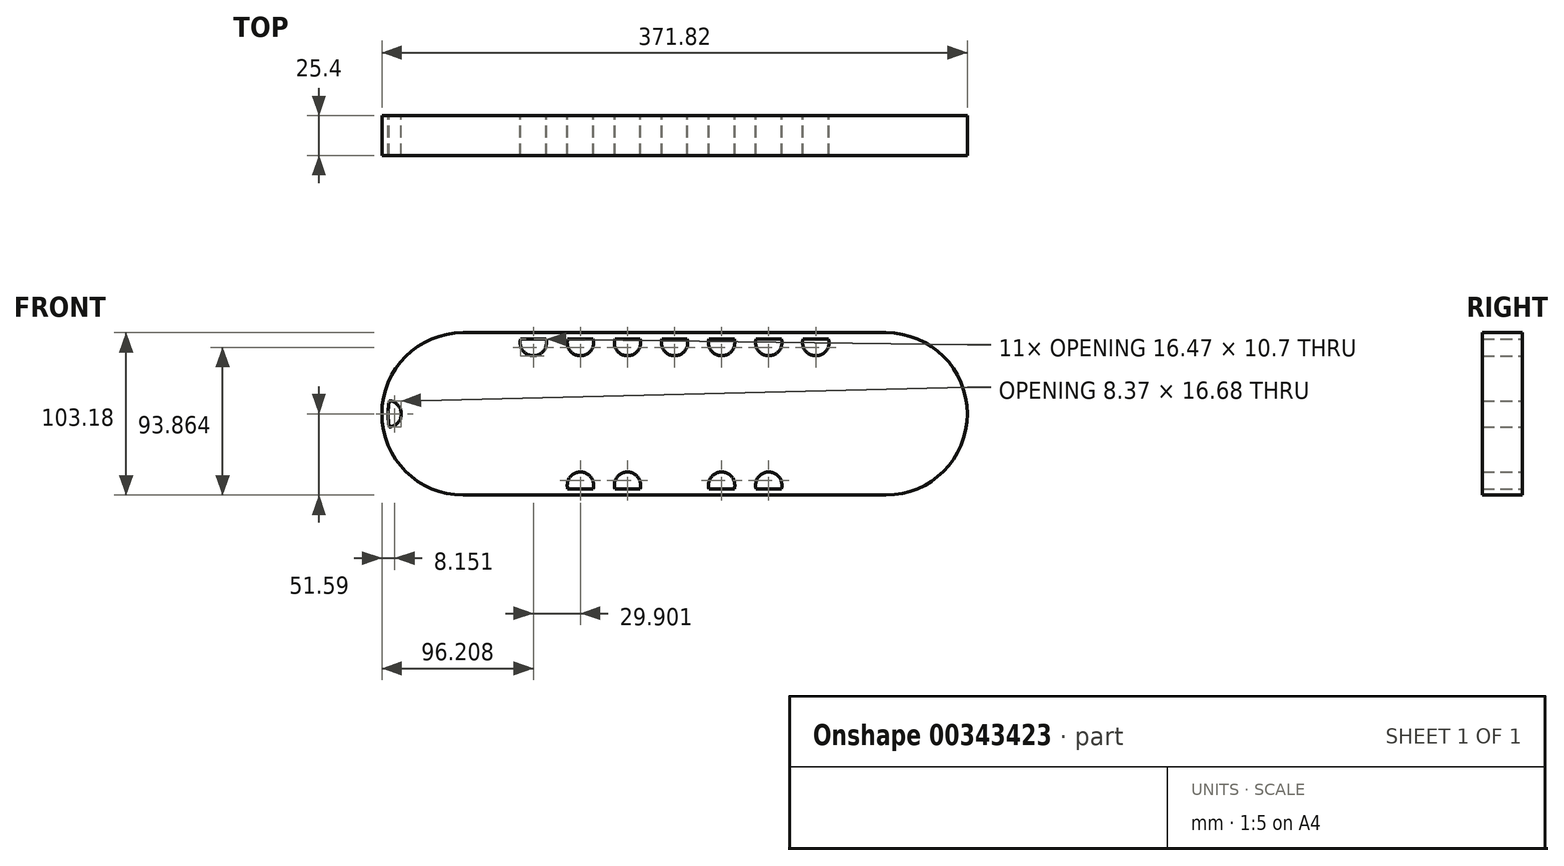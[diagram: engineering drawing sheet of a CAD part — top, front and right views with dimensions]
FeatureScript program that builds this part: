
annotation { "Feature Type Name" : "Feature", "Feature Type Description" : "" }
export const myFeature = defineFeature(function(context is Context, id is Id, definition is map)
    precondition{}
    {
        {
            var Q0;
            Q0=qCreatedBy(makeId("Front.planeOp"),FACE);
            var sketch = newSketch(context, id + "F0", { "sketchPlane" : qUnion([Q0])});
            skCircle(sketch, "E0", {"center": v(0, 0) * mm, "radius": 9.53 * mm});
            skCircle(sketch, "E1", {"center": v(0, 0) * mm, "radius": 15.88 * mm});
            skCircle(sketch, "E2", {"center": v(0, 0) * mm, "radius": 25.4 * mm});
            skCircle(sketch, "E3", {"center": v(0, 0) * mm, "radius": 38.1 * mm});
            skArc(sketch, "E4", {"start": v(5.87, 47.26) * mm, "mid": v(0, 47.63) * mm, "end": v(-5.87, 47.26) * mm});
            skLineSegment(sketch, "E5", {"start": v(-5.87, 47.26) * mm, "end": v(-7.62, 37.33) * mm});
            skLineSegment(sketch, "E6", {"start": v(5.87, 47.26) * mm, "end": v(7.62, 37.33) * mm});
            skLineSegment(sketch, "E7.1.0", {"start": v(-32.53, 34.79) * mm, "end": v(-28.1, 25.72) * mm});
            skArc(sketch, "E7.1.1", {"start": v(-23.03, 41.69) * mm, "mid": v(-28, 38.53) * mm, "end": v(-32.53, 34.79) * mm});
            skLineSegment(sketch, "E7.1.2", {"start": v(-23.03, 41.69) * mm, "end": v(-15.78, 34.68) * mm});
            skLineSegment(sketch, "E7.2.0", {"start": v(-46.76, 9.02) * mm, "end": v(-37.86, 4.29) * mm});
            skArc(sketch, "E7.2.1", {"start": v(-43.14, 20.19) * mm, "mid": v(-45.3, 14.72) * mm, "end": v(-46.76, 9.02) * mm});
            skLineSegment(sketch, "E7.2.2", {"start": v(-43.14, 20.19) * mm, "end": v(-33.15, 18.78) * mm});
            skLineSegment(sketch, "E7.3.0", {"start": v(-43.14, -20.19) * mm, "end": v(-33.15, -18.78) * mm});
            skArc(sketch, "E7.3.1", {"start": v(-46.76, -9.02) * mm, "mid": v(-45.3, -14.72) * mm, "end": v(-43.14, -20.19) * mm});
            skLineSegment(sketch, "E7.3.2", {"start": v(-46.76, -9.02) * mm, "end": v(-37.86, -4.29) * mm});
            skLineSegment(sketch, "E7.4.0", {"start": v(-23.03, -41.69) * mm, "end": v(-15.78, -34.68) * mm});
            skArc(sketch, "E7.4.1", {"start": v(-32.53, -34.79) * mm, "mid": v(-28, -38.53) * mm, "end": v(-23.03, -41.69) * mm});
            skLineSegment(sketch, "E7.4.2", {"start": v(-32.53, -34.79) * mm, "end": v(-28.1, -25.72) * mm});
            skLineSegment(sketch, "E7.5.0", {"start": v(5.87, -47.26) * mm, "end": v(7.62, -37.33) * mm});
            skArc(sketch, "E7.5.1", {"start": v(-5.87, -47.26) * mm, "mid": v(0, -47.63) * mm, "end": v(5.87, -47.26) * mm});
            skLineSegment(sketch, "E7.5.2", {"start": v(-5.87, -47.26) * mm, "end": v(-7.62, -37.33) * mm});
            skLineSegment(sketch, "E7.6.0", {"start": v(32.53, -34.79) * mm, "end": v(28.1, -25.72) * mm});
            skArc(sketch, "E7.6.1", {"start": v(23.03, -41.69) * mm, "mid": v(28, -38.53) * mm, "end": v(32.53, -34.79) * mm});
            skLineSegment(sketch, "E7.6.2", {"start": v(23.03, -41.69) * mm, "end": v(15.78, -34.68) * mm});
            skLineSegment(sketch, "E7.7.0", {"start": v(46.76, -9.02) * mm, "end": v(37.86, -4.29) * mm});
            skArc(sketch, "E7.7.1", {"start": v(43.14, -20.19) * mm, "mid": v(45.3, -14.72) * mm, "end": v(46.76, -9.02) * mm});
            skLineSegment(sketch, "E7.7.2", {"start": v(43.14, -20.19) * mm, "end": v(33.15, -18.78) * mm});
            skLineSegment(sketch, "E7.8.0", {"start": v(43.14, 20.19) * mm, "end": v(33.15, 18.78) * mm});
            skArc(sketch, "E7.8.1", {"start": v(46.76, 9.02) * mm, "mid": v(45.3, 14.72) * mm, "end": v(43.14, 20.19) * mm});
            skLineSegment(sketch, "E7.8.2", {"start": v(46.76, 9.02) * mm, "end": v(37.86, 4.29) * mm});
            skLineSegment(sketch, "E7.9.0", {"start": v(23.03, 41.69) * mm, "end": v(15.78, 34.68) * mm});
            skArc(sketch, "E7.9.1", {"start": v(32.53, 34.79) * mm, "mid": v(28, 38.53) * mm, "end": v(23.03, 41.69) * mm});
            skLineSegment(sketch, "E7.9.2", {"start": v(32.53, 34.79) * mm, "end": v(28.1, 25.72) * mm});
            skLineSegment(sketch, "E8", {"start": v(-3.98, 25.09) * mm, "end": v(-3.98, 15.37) * mm});
            skLineSegment(sketch, "E9", {"start": v(3.98, 25.09) * mm, "end": v(3.98, 15.37) * mm});
            skLineSegment(sketch, "E10.1.0", {"start": v(-19.74, -15.99) * mm, "end": v(-11.32, -11.13) * mm});
            skLineSegment(sketch, "E10.1.1", {"start": v(-23.71, -9.1) * mm, "end": v(-15.3, -4.24) * mm});
            skLineSegment(sketch, "E10.2.0", {"start": v(23.71, -9.1) * mm, "end": v(15.3, -4.24) * mm});
            skLineSegment(sketch, "E10.2.1", {"start": v(19.74, -15.99) * mm, "end": v(11.32, -11.13) * mm});
            skSolve(sketch);
        }
        {
            var Q0;
            Q0=qCreatedBy(makeId("Front.planeOp"),FACE);
            var sketch = newSketch(context, id + "F1", { "sketchPlane" : qUnion([Q0])});
            skArc(sketch, "E11", {"start": v(23.03, 41.69) * mm, "mid": v(-10.34, 46.49) * mm, "end": v(-38.53, 28) * mm});
            skLineSegment(sketch, "E12.0", {"start": v(23.03, 41.69) * mm, "end": v(15.78, 34.68) * mm, "construction": true});
            skLineSegment(sketch, "E12.1", {"start": v(5.87, 47.26) * mm, "end": v(7.62, 37.33) * mm, "construction": true});
            skLineSegment(sketch, "E12.2", {"start": v(-5.87, 47.26) * mm, "end": v(-7.62, 37.33) * mm, "construction": true});
            skLineSegment(sketch, "E12.3", {"start": v(-23.03, 41.69) * mm, "end": v(-15.78, 34.68) * mm, "construction": true});
            skLineSegment(sketch, "E12.4", {"start": v(-32.53, 34.79) * mm, "end": v(-28.1, 25.72) * mm, "construction": true});
            skLineSegment(sketch, "E12.5", {"start": v(-43.14, 20.19) * mm, "end": v(-33.15, 18.78) * mm, "construction": true});
            skLineSegment(sketch, "E12.6", {"start": v(-46.76, 9.02) * mm, "end": v(-37.86, 4.29) * mm, "construction": true});
            skLineSegment(sketch, "E12.7", {"start": v(-46.76, -9.02) * mm, "end": v(-37.86, -4.29) * mm, "construction": true});
            skLineSegment(sketch, "E13.0", {"start": v(-3.98, 25.09) * mm, "end": v(-3.98, 15.37) * mm, "construction": true});
            skLineSegment(sketch, "E13.1", {"start": v(3.98, 25.09) * mm, "end": v(3.98, 15.37) * mm, "construction": true});
            skLineSegment(sketch, "E13.2", {"start": v(23.71, -9.1) * mm, "end": v(15.3, -4.24) * mm, "construction": true});
            skLineSegment(sketch, "E13.3", {"start": v(19.74, -15.99) * mm, "end": v(11.32, -11.13) * mm, "construction": true});
            skLineSegment(sketch, "E13.4", {"start": v(-19.74, -15.99) * mm, "end": v(-11.32, -11.13) * mm, "construction": true});
            skLineSegment(sketch, "E13.5", {"start": v(-23.71, -9.1) * mm, "end": v(-15.3, -4.24) * mm, "construction": true});
            skCircle(sketch, "E14", {"center": v(14.72, 45.3) * mm, "radius": 8.37 * mm});
            skCircle(sketch, "E15", {"center": v(-14.72, 45.3) * mm, "radius": 8.37 * mm});
            skCircle(sketch, "E16", {"center": v(-38.53, 28) * mm, "radius": 8.37 * mm});
            skCircle(sketch, "E17", {"center": v(-47.62, 0) * mm, "radius": 8.37 * mm});
            skLineSegment(sketch, "E18", {"start": v(-14.72, 45.3) * mm, "end": v(14.72, 45.3) * mm, "construction": true});
            skArc(sketch, "E19.trimOffspring", {"start": v(-47.62, 0) * mm, "mid": v(-24.2, -41.02) * mm, "end": v(23.03, -41.69) * mm});
            skArc(sketch, "E20.trimOffspring", {"start": v(-42.84, 20.81) * mm, "mid": v(-45.3, 14.72) * mm, "end": v(-46.89, 8.34) * mm});
            skLineSegment(sketch, "E21", {"start": v(14.72, 45.3) * mm, "end": v(44.62, 45.3) * mm, "construction": true});
            skLineSegment(sketch, "E22", {"start": v(44.62, 45.3) * mm, "end": v(74.52, 45.3) * mm, "construction": true});
            skLineSegment(sketch, "E23", {"start": v(74.52, 45.3) * mm, "end": v(104.42, 45.3) * mm, "construction": true});
            skLineSegment(sketch, "E24", {"start": v(104.42, 45.3) * mm, "end": v(134.32, 45.3) * mm, "construction": true});
            skCircle(sketch, "E25", {"center": v(44.62, 45.3) * mm, "radius": 8.37 * mm});
            skCircle(sketch, "E26", {"center": v(74.52, 45.3) * mm, "radius": 8.37 * mm});
            skCircle(sketch, "E27", {"center": v(104.42, 45.3) * mm, "radius": 8.37 * mm});
            skCircle(sketch, "E28", {"center": v(134.32, 45.3) * mm, "radius": 8.37 * mm});
            skPoint(sketch, "E29", {"position": v(23.09, 45.3) * mm});
            skPoint(sketch, "E30", {"position": v(36.25, 45.3) * mm});
            skLineSegment(sketch, "E31", {"start": v(0, 0) * mm, "end": v(134.32, 0) * mm, "construction": true});
            skLineSegment(sketch, "E32", {"start": v(134.32, 45.3) * mm, "end": v(134.32, 0) * mm, "construction": true});
            skCircle(sketch, "E33.MirrorC", {"center": v(134.32, -45.3) * mm, "radius": 8.37 * mm});
            skCircle(sketch, "E34.MirrorC", {"center": v(104.42, -45.3) * mm, "radius": 8.37 * mm});
            skCircle(sketch, "E35.MirrorC", {"center": v(74.52, -45.3) * mm, "radius": 8.37 * mm});
            skCircle(sketch, "E36.MirrorC", {"center": v(44.62, -45.3) * mm, "radius": 8.37 * mm});
            skCircle(sketch, "E37.MirrorC", {"center": v(14.72, -45.3) * mm, "radius": 8.37 * mm});
            skCircle(sketch, "E38.MirrorC", {"center": v(-14.72, -45.3) * mm, "radius": 8.37 * mm});
            skCircle(sketch, "E39.MirrorC", {"center": v(-38.53, -28) * mm, "radius": 8.37 * mm});
            skCircle(sketch, "E40.MirrorC", {"center": v(164.22, -45.3) * mm, "radius": 8.37 * mm});
            skCircle(sketch, "E41.MirrorC", {"center": v(194.12, -45.3) * mm, "radius": 8.37 * mm});
            skCircle(sketch, "E42.MirrorC", {"center": v(224.03, -45.3) * mm, "radius": 8.37 * mm});
            skCircle(sketch, "E43.MirrorC", {"center": v(253.93, -45.3) * mm, "radius": 8.37 * mm});
            skCircle(sketch, "E44.MirrorC", {"center": v(283.36, -45.3) * mm, "radius": 8.37 * mm});
            skCircle(sketch, "E45.MirrorC", {"center": v(307.17, -28) * mm, "radius": 8.37 * mm});
            skCircle(sketch, "E46.MirrorC", {"center": v(316.27, 0) * mm, "radius": 8.37 * mm});
            skCircle(sketch, "E47.MirrorC", {"center": v(307.17, 28) * mm, "radius": 8.37 * mm});
            skCircle(sketch, "E48.MirrorC", {"center": v(283.36, 45.3) * mm, "radius": 8.37 * mm});
            skCircle(sketch, "E49.MirrorC", {"center": v(253.93, 45.3) * mm, "radius": 8.37 * mm});
            skCircle(sketch, "E50.MirrorC", {"center": v(224.03, 45.3) * mm, "radius": 8.37 * mm});
            skCircle(sketch, "E51.MirrorC", {"center": v(194.12, 45.3) * mm, "radius": 8.37 * mm});
            skCircle(sketch, "E52.MirrorC", {"center": v(164.22, 45.3) * mm, "radius": 8.37 * mm});
            skSolve(sketch);
        }
        {
            var Q0;
            Q0=qCreatedBy(makeId("Front.planeOp"),FACE);
            var sketch = newSketch(context, id + "F2", { "sketchPlane" : qUnion([Q0])});
            skArc(sketch, "E53", {"start": v(0, 47.62) * mm, "mid": v(-47.62, 0) * mm, "end": v(0, -47.62) * mm});
            skLineSegment(sketch, "E54", {"start": v(0, 47.62) * mm, "end": v(268.64, 47.62) * mm});
            skLineSegment(sketch, "E55", {"start": v(0, -47.62) * mm, "end": v(268.64, -47.62) * mm});
            skLineSegment(sketch, "E56.0", {"start": v(134.32, 45.3) * mm, "end": v(134.32, 0) * mm, "construction": true});
            skLineSegment(sketch, "E56.1", {"start": v(0, 0) * mm, "end": v(134.32, 0) * mm, "construction": true});
            skLineSegment(sketch, "E57.MirrorCS", {"start": v(268.64, 0) * mm, "end": v(134.32, 0) * mm, "construction": true});
            skArc(sketch, "E58", {"start": v(268.64, -47.62) * mm, "mid": v(316.27, 0) * mm, "end": v(268.64, 47.62) * mm});
            skLineSegment(sketch, "E59.0", {"start": v(0, 51.59) * mm, "end": v(268.64, 51.59) * mm});
            skArc(sketch, "E59.1", {"start": v(0, 51.59) * mm, "mid": v(-51.59, 0) * mm, "end": v(0, -51.59) * mm});
            skLineSegment(sketch, "E59.2", {"start": v(0, -51.59) * mm, "end": v(268.64, -51.59) * mm});
            skArc(sketch, "E59.3", {"start": v(268.64, -51.59) * mm, "mid": v(320.23, 0) * mm, "end": v(268.64, 51.59) * mm});
            skArc(sketch, "E60.0", {"start": v(69, 51.59) * mm, "mid": v(74.52, 36.92) * mm, "end": v(80.04, 51.59) * mm});
            skArc(sketch, "E60.1", {"start": v(98.9, 51.59) * mm, "mid": v(104.42, 36.92) * mm, "end": v(109.94, 51.59) * mm});
            skArc(sketch, "E60.2", {"start": v(139.84, 51.59) * mm, "mid": v(134.32, 36.92) * mm, "end": v(128.8, 51.59) * mm});
            skArc(sketch, "E60.3", {"start": v(169.74, 51.59) * mm, "mid": v(164.22, 36.92) * mm, "end": v(158.7, 51.59) * mm});
            skArc(sketch, "E60.4", {"start": v(199.65, 51.59) * mm, "mid": v(194.12, 36.92) * mm, "end": v(188.6, 51.59) * mm});
            skArc(sketch, "E60.5", {"start": v(229.55, 51.59) * mm, "mid": v(224.03, 36.92) * mm, "end": v(218.5, 51.59) * mm});
            skArc(sketch, "E60.6", {"start": v(259.45, 51.59) * mm, "mid": v(253.93, 36.92) * mm, "end": v(248.4, 51.59) * mm});
            skArc(sketch, "E60.7", {"start": v(39.1, 51.59) * mm, "mid": v(44.62, 36.92) * mm, "end": v(50.14, 51.59) * mm});
            skArc(sketch, "E60.8", {"start": v(9.2, 51.59) * mm, "mid": v(14.72, 36.92) * mm, "end": v(20.24, 51.59) * mm});
            skArc(sketch, "E60.9", {"start": v(-23.04, 46.15) * mm, "mid": v(-12.13, 37.33) * mm, "end": v(-8.49, 50.88) * mm});
            skArc(sketch, "E60.10", {"start": v(-45.77, 23.8) * mm, "mid": v(-31.76, 23.07) * mm, "end": v(-36.77, 36.18) * mm});
            skArc(sketch, "E60.11", {"start": v(-51.02, -7.65) * mm, "mid": v(-39.25, 0) * mm, "end": v(-51.02, 7.65) * mm});
            skArc(sketch, "E60.12", {"start": v(-45.77, -23.8) * mm, "mid": v(-31.76, -23.07) * mm, "end": v(-36.77, -36.18) * mm});
            skArc(sketch, "E60.13", {"start": v(9.2, -51.59) * mm, "mid": v(14.72, -36.92) * mm, "end": v(20.24, -51.59) * mm});
            skArc(sketch, "E60.14", {"start": v(39.1, -51.59) * mm, "mid": v(44.62, -36.92) * mm, "end": v(50.14, -51.59) * mm});
            skArc(sketch, "E60.15", {"start": v(69, -51.59) * mm, "mid": v(74.52, -36.92) * mm, "end": v(80.04, -51.59) * mm});
            skArc(sketch, "E60.16", {"start": v(98.9, -51.59) * mm, "mid": v(104.42, -36.92) * mm, "end": v(109.94, -51.59) * mm});
            skArc(sketch, "E60.17", {"start": v(128.8, -51.59) * mm, "mid": v(134.32, -36.92) * mm, "end": v(139.84, -51.59) * mm});
            skArc(sketch, "E60.18", {"start": v(169.74, -51.59) * mm, "mid": v(164.22, -36.92) * mm, "end": v(158.7, -51.59) * mm});
            skArc(sketch, "E60.19", {"start": v(229.55, -51.59) * mm, "mid": v(224.03, -36.92) * mm, "end": v(218.5, -51.59) * mm});
            skArc(sketch, "E60.20", {"start": v(259.45, -51.59) * mm, "mid": v(253.93, -36.92) * mm, "end": v(248.4, -51.59) * mm});
            skArc(sketch, "E60.21", {"start": v(291.69, -46.15) * mm, "mid": v(280.77, -37.33) * mm, "end": v(277.13, -50.88) * mm});
            skArc(sketch, "E60.22", {"start": v(199.65, -51.59) * mm, "mid": v(194.12, -36.92) * mm, "end": v(188.6, -51.59) * mm});
            skArc(sketch, "E60.23", {"start": v(314.42, -23.8) * mm, "mid": v(300.4, -23.07) * mm, "end": v(305.42, -36.18) * mm});
            skArc(sketch, "E60.24", {"start": v(319.66, -7.65) * mm, "mid": v(307.9, 0) * mm, "end": v(319.66, 7.65) * mm});
            skArc(sketch, "E60.25", {"start": v(314.42, 23.8) * mm, "mid": v(300.4, 23.07) * mm, "end": v(305.42, 36.18) * mm});
            skArc(sketch, "E60.26", {"start": v(291.69, 46.15) * mm, "mid": v(280.77, 37.33) * mm, "end": v(277.13, 50.88) * mm});
            skArc(sketch, "E60.27", {"start": v(-23.04, -46.15) * mm, "mid": v(-12.13, -37.33) * mm, "end": v(-8.49, -50.88) * mm});
            skSolve(sketch);
        }
        {
            var Q0;
            Q0 = qSketchRegion(id + "F2", true);
            var Q1;
            {var subQ0=sQuery(id+"F2.wireOp",EDGE,"E60.11");var subQ1=sQuery(id+"F2.wireOp",EDGE,"E53");var subQ2=makeQuery(id+"F2.imprint","INTERSECT",VERTEX,{"disambiguationData":[OD(0.0)],"derivedFrom":[subQ1,subQ0]});Q1=makeQuery(id+"F2.imprint","IMPRINT",FACE,{"disambiguationData":[TD([[makeQuery(id+"F2.imprint","IMPRINT",EDGE,{"disambiguationData":[TD([[subQ2,-1.0]])],"derivedFrom":subQ1}),1.0]])]});}
            var Q2;
            {var subQ0=sQuery(id+"F2.wireOp",EDGE,"E60.12");var subQ1=sQuery(id+"F2.wireOp",EDGE,"E53");var subQ2=makeQuery(id+"F2.imprint","INTERSECT",VERTEX,{"disambiguationData":[OD(0.0)],"derivedFrom":[subQ1,subQ0]});Q2=makeQuery(id+"F2.imprint","IMPRINT",FACE,{"disambiguationData":[TD([[makeQuery(id+"F2.imprint","IMPRINT",EDGE,{"disambiguationData":[TD([[subQ2,-1.0]])],"derivedFrom":subQ1}),1.0]])]});}
            var Q3;
            {var subQ0=sQuery(id+"F2.wireOp",EDGE,"E60.27");var subQ1=sQuery(id+"F2.wireOp",EDGE,"E53");var subQ2=makeQuery(id+"F2.imprint","INTERSECT",VERTEX,{"disambiguationData":[OD(0.0)],"derivedFrom":[subQ1,subQ0]});Q3=makeQuery(id+"F2.imprint","IMPRINT",FACE,{"disambiguationData":[TD([[makeQuery(id+"F2.imprint","IMPRINT",EDGE,{"disambiguationData":[TD([[subQ2,-1.0]])],"derivedFrom":subQ1}),1.0]])]});}
            var Q4;
            {var subQ0=sQuery(id+"F2.wireOp",EDGE,"E60.13");var subQ1=sQuery(id+"F2.wireOp",EDGE,"E55");var subQ2=makeQuery(id+"F2.imprint","INTERSECT",VERTEX,{"disambiguationData":[OD(0.0)],"derivedFrom":[subQ1,subQ0]});Q4=makeQuery(id+"F2.imprint","IMPRINT",FACE,{"disambiguationData":[TD([[makeQuery(id+"F2.imprint","IMPRINT",EDGE,{"disambiguationData":[TD([[subQ2,-1.0]])],"derivedFrom":subQ1}),1.0]])]});}
            var Q5;
            {var subQ0=sQuery(id+"F2.wireOp",EDGE,"E60.14");var subQ1=sQuery(id+"F2.wireOp",EDGE,"E55");var subQ2=makeQuery(id+"F2.imprint","INTERSECT",VERTEX,{"disambiguationData":[OD(0.0)],"derivedFrom":[subQ1,subQ0]});Q5=makeQuery(id+"F2.imprint","IMPRINT",FACE,{"disambiguationData":[TD([[makeQuery(id+"F2.imprint","IMPRINT",EDGE,{"disambiguationData":[TD([[subQ2,-1.0]])],"derivedFrom":subQ1}),1.0]])]});}
            var Q6;
            {var subQ0=sQuery(id+"F2.wireOp",EDGE,"E60.15");var subQ1=sQuery(id+"F2.wireOp",EDGE,"E55");var subQ2=makeQuery(id+"F2.imprint","INTERSECT",VERTEX,{"disambiguationData":[OD(0.0)],"derivedFrom":[subQ1,subQ0]});Q6=makeQuery(id+"F2.imprint","IMPRINT",FACE,{"disambiguationData":[TD([[makeQuery(id+"F2.imprint","IMPRINT",EDGE,{"disambiguationData":[TD([[subQ2,-1.0]])],"derivedFrom":subQ1}),1.0]])]});}
            var Q7;
            {var subQ0=sQuery(id+"F2.wireOp",EDGE,"E60.16");var subQ1=sQuery(id+"F2.wireOp",EDGE,"E55");var subQ2=makeQuery(id+"F2.imprint","INTERSECT",VERTEX,{"disambiguationData":[OD(0.0)],"derivedFrom":[subQ1,subQ0]});Q7=makeQuery(id+"F2.imprint","IMPRINT",FACE,{"disambiguationData":[TD([[makeQuery(id+"F2.imprint","IMPRINT",EDGE,{"disambiguationData":[TD([[subQ2,-1.0]])],"derivedFrom":subQ1}),1.0]])]});}
            var Q8;
            {var subQ0=sQuery(id+"F2.wireOp",EDGE,"E60.17");var subQ1=sQuery(id+"F2.wireOp",EDGE,"E55");var subQ2=makeQuery(id+"F2.imprint","INTERSECT",VERTEX,{"disambiguationData":[OD(0.0)],"derivedFrom":[subQ1,subQ0]});Q8=makeQuery(id+"F2.imprint","IMPRINT",FACE,{"disambiguationData":[TD([[makeQuery(id+"F2.imprint","IMPRINT",EDGE,{"disambiguationData":[TD([[subQ2,-1.0]])],"derivedFrom":subQ1}),1.0]])]});}
            var Q9;
            {var subQ0=sQuery(id+"F2.wireOp",EDGE,"E60.18");var subQ1=sQuery(id+"F2.wireOp",EDGE,"E55");var subQ2=makeQuery(id+"F2.imprint","INTERSECT",VERTEX,{"disambiguationData":[OD(0.0)],"derivedFrom":[subQ1,subQ0]});Q9=makeQuery(id+"F2.imprint","IMPRINT",FACE,{"disambiguationData":[TD([[makeQuery(id+"F2.imprint","IMPRINT",EDGE,{"disambiguationData":[TD([[subQ2,-1.0]])],"derivedFrom":subQ1}),1.0]])]});}
            var Q10;
            {var subQ0=sQuery(id+"F2.wireOp",EDGE,"E60.22");var subQ1=sQuery(id+"F2.wireOp",EDGE,"E55");var subQ2=makeQuery(id+"F2.imprint","INTERSECT",VERTEX,{"disambiguationData":[OD(0.0)],"derivedFrom":[subQ1,subQ0]});Q10=makeQuery(id+"F2.imprint","IMPRINT",FACE,{"disambiguationData":[TD([[makeQuery(id+"F2.imprint","IMPRINT",EDGE,{"disambiguationData":[TD([[subQ2,-1.0]])],"derivedFrom":subQ1}),1.0]])]});}
            var Q11;
            {var subQ0=sQuery(id+"F2.wireOp",EDGE,"E60.19");var subQ1=sQuery(id+"F2.wireOp",EDGE,"E55");var subQ2=makeQuery(id+"F2.imprint","INTERSECT",VERTEX,{"disambiguationData":[OD(0.0)],"derivedFrom":[subQ1,subQ0]});Q11=makeQuery(id+"F2.imprint","IMPRINT",FACE,{"disambiguationData":[TD([[makeQuery(id+"F2.imprint","IMPRINT",EDGE,{"disambiguationData":[TD([[subQ2,-1.0]])],"derivedFrom":subQ1}),1.0]])]});}
            var Q12;
            {var subQ0=sQuery(id+"F2.wireOp",EDGE,"E60.20");var subQ1=sQuery(id+"F2.wireOp",EDGE,"E55");var subQ2=makeQuery(id+"F2.imprint","INTERSECT",VERTEX,{"disambiguationData":[OD(0.0)],"derivedFrom":[subQ1,subQ0]});Q12=makeQuery(id+"F2.imprint","IMPRINT",FACE,{"disambiguationData":[TD([[makeQuery(id+"F2.imprint","IMPRINT",EDGE,{"disambiguationData":[TD([[subQ2,-1.0]])],"derivedFrom":subQ1}),1.0]])]});}
            var Q13;
            {var subQ0=sQuery(id+"F2.wireOp",EDGE,"E60.21");var subQ1=sQuery(id+"F2.wireOp",EDGE,"E58");var subQ2=makeQuery(id+"F2.imprint","INTERSECT",VERTEX,{"disambiguationData":[OD(0.0)],"derivedFrom":[subQ1,subQ0]});Q13=makeQuery(id+"F2.imprint","IMPRINT",FACE,{"disambiguationData":[TD([[makeQuery(id+"F2.imprint","IMPRINT",EDGE,{"disambiguationData":[TD([[subQ2,-1.0]])],"derivedFrom":subQ1}),1.0]])]});}
            var Q14;
            {var subQ0=sQuery(id+"F2.wireOp",EDGE,"E60.24");var subQ1=sQuery(id+"F2.wireOp",EDGE,"E58");var subQ2=makeQuery(id+"F2.imprint","INTERSECT",VERTEX,{"disambiguationData":[OD(0.0)],"derivedFrom":[subQ1,subQ0]});Q14=makeQuery(id+"F2.imprint","IMPRINT",FACE,{"disambiguationData":[TD([[makeQuery(id+"F2.imprint","IMPRINT",EDGE,{"disambiguationData":[TD([[subQ2,-1.0]])],"derivedFrom":subQ1}),1.0]])]});}
            var Q15;
            {var subQ0=sQuery(id+"F2.wireOp",EDGE,"E60.6");var subQ1=sQuery(id+"F2.wireOp",EDGE,"E54");var subQ2=makeQuery(id+"F2.imprint","INTERSECT",VERTEX,{"disambiguationData":[OD(0.0)],"derivedFrom":[subQ1,subQ0]});Q15=makeQuery(id+"F2.imprint","IMPRINT",FACE,{"disambiguationData":[TD([[makeQuery(id+"F2.imprint","IMPRINT",EDGE,{"disambiguationData":[TD([[subQ2,-1.0]])],"derivedFrom":subQ1}),-1.0]])]});}
            var Q16;
            {var subQ0=sQuery(id+"F2.wireOp",EDGE,"E60.23");var subQ1=sQuery(id+"F2.wireOp",EDGE,"E58");var subQ2=makeQuery(id+"F2.imprint","INTERSECT",VERTEX,{"disambiguationData":[OD(0.0)],"derivedFrom":[subQ1,subQ0]});Q16=makeQuery(id+"F2.imprint","IMPRINT",FACE,{"disambiguationData":[TD([[makeQuery(id+"F2.imprint","IMPRINT",EDGE,{"disambiguationData":[TD([[subQ2,-1.0]])],"derivedFrom":subQ1}),1.0]])]});}
            var Q17;
            {var subQ0=sQuery(id+"F2.wireOp",EDGE,"E60.25");var subQ1=sQuery(id+"F2.wireOp",EDGE,"E58");var subQ2=makeQuery(id+"F2.imprint","INTERSECT",VERTEX,{"disambiguationData":[OD(0.0)],"derivedFrom":[subQ1,subQ0]});Q17=makeQuery(id+"F2.imprint","IMPRINT",FACE,{"disambiguationData":[TD([[makeQuery(id+"F2.imprint","IMPRINT",EDGE,{"disambiguationData":[TD([[subQ2,-1.0]])],"derivedFrom":subQ1}),1.0]])]});}
            var Q18;
            {var subQ0=sQuery(id+"F2.wireOp",EDGE,"E60.26");var subQ1=sQuery(id+"F2.wireOp",EDGE,"E58");var subQ2=makeQuery(id+"F2.imprint","INTERSECT",VERTEX,{"disambiguationData":[OD(0.0)],"derivedFrom":[subQ1,subQ0]});Q18=makeQuery(id+"F2.imprint","IMPRINT",FACE,{"disambiguationData":[TD([[makeQuery(id+"F2.imprint","IMPRINT",EDGE,{"disambiguationData":[TD([[subQ2,-1.0]])],"derivedFrom":subQ1}),1.0]])]});}
            var Q19;
            {var subQ0=sQuery(id+"F2.wireOp",EDGE,"E60.5");var subQ1=sQuery(id+"F2.wireOp",EDGE,"E54");var subQ2=makeQuery(id+"F2.imprint","INTERSECT",VERTEX,{"disambiguationData":[OD(0.0)],"derivedFrom":[subQ1,subQ0]});Q19=makeQuery(id+"F2.imprint","IMPRINT",FACE,{"disambiguationData":[TD([[makeQuery(id+"F2.imprint","IMPRINT",EDGE,{"disambiguationData":[TD([[subQ2,-1.0]])],"derivedFrom":subQ1}),-1.0]])]});}
            var Q20;
            {var subQ0=sQuery(id+"F2.wireOp",EDGE,"E60.4");var subQ1=sQuery(id+"F2.wireOp",EDGE,"E54");var subQ2=makeQuery(id+"F2.imprint","INTERSECT",VERTEX,{"disambiguationData":[OD(0.0)],"derivedFrom":[subQ1,subQ0]});Q20=makeQuery(id+"F2.imprint","IMPRINT",FACE,{"disambiguationData":[TD([[makeQuery(id+"F2.imprint","IMPRINT",EDGE,{"disambiguationData":[TD([[subQ2,-1.0]])],"derivedFrom":subQ1}),-1.0]])]});}
            var Q21;
            {var subQ0=sQuery(id+"F2.wireOp",EDGE,"E60.3");var subQ1=sQuery(id+"F2.wireOp",EDGE,"E54");var subQ2=makeQuery(id+"F2.imprint","INTERSECT",VERTEX,{"disambiguationData":[OD(0.0)],"derivedFrom":[subQ1,subQ0]});Q21=makeQuery(id+"F2.imprint","IMPRINT",FACE,{"disambiguationData":[TD([[makeQuery(id+"F2.imprint","IMPRINT",EDGE,{"disambiguationData":[TD([[subQ2,-1.0]])],"derivedFrom":subQ1}),-1.0]])]});}
            var Q22;
            {var subQ0=sQuery(id+"F2.wireOp",EDGE,"E60.2");var subQ1=sQuery(id+"F2.wireOp",EDGE,"E54");var subQ2=makeQuery(id+"F2.imprint","INTERSECT",VERTEX,{"disambiguationData":[OD(0.0)],"derivedFrom":[subQ1,subQ0]});Q22=makeQuery(id+"F2.imprint","IMPRINT",FACE,{"disambiguationData":[TD([[makeQuery(id+"F2.imprint","IMPRINT",EDGE,{"disambiguationData":[TD([[subQ2,-1.0]])],"derivedFrom":subQ1}),-1.0]])]});}
            var Q23;
            {var subQ0=sQuery(id+"F2.wireOp",EDGE,"E60.1");var subQ1=sQuery(id+"F2.wireOp",EDGE,"E54");var subQ2=makeQuery(id+"F2.imprint","INTERSECT",VERTEX,{"disambiguationData":[OD(0.0)],"derivedFrom":[subQ1,subQ0]});Q23=makeQuery(id+"F2.imprint","IMPRINT",FACE,{"disambiguationData":[TD([[makeQuery(id+"F2.imprint","IMPRINT",EDGE,{"disambiguationData":[TD([[subQ2,-1.0]])],"derivedFrom":subQ1}),-1.0]])]});}
            var Q24;
            {var subQ0=sQuery(id+"F2.wireOp",EDGE,"E60.7");var subQ1=sQuery(id+"F2.wireOp",EDGE,"E54");var subQ2=makeQuery(id+"F2.imprint","INTERSECT",VERTEX,{"disambiguationData":[OD(0.0)],"derivedFrom":[subQ1,subQ0]});Q24=makeQuery(id+"F2.imprint","IMPRINT",FACE,{"disambiguationData":[TD([[makeQuery(id+"F2.imprint","IMPRINT",EDGE,{"disambiguationData":[TD([[subQ2,-1.0]])],"derivedFrom":subQ1}),-1.0]])]});}
            var Q25;
            {var subQ0=sQuery(id+"F2.wireOp",EDGE,"E60.8");var subQ1=sQuery(id+"F2.wireOp",EDGE,"E54");var subQ2=makeQuery(id+"F2.imprint","INTERSECT",VERTEX,{"disambiguationData":[OD(0.0)],"derivedFrom":[subQ1,subQ0]});Q25=makeQuery(id+"F2.imprint","IMPRINT",FACE,{"disambiguationData":[TD([[makeQuery(id+"F2.imprint","IMPRINT",EDGE,{"disambiguationData":[TD([[subQ2,-1.0]])],"derivedFrom":subQ1}),-1.0]])]});}
            var Q26;
            {var subQ0=sQuery(id+"F2.wireOp",EDGE,"E60.9");var subQ1=sQuery(id+"F2.wireOp",EDGE,"E53");var subQ2=makeQuery(id+"F2.imprint","INTERSECT",VERTEX,{"disambiguationData":[OD(0.0)],"derivedFrom":[subQ1,subQ0]});Q26=makeQuery(id+"F2.imprint","IMPRINT",FACE,{"disambiguationData":[TD([[makeQuery(id+"F2.imprint","IMPRINT",EDGE,{"disambiguationData":[TD([[subQ2,-1.0]])],"derivedFrom":subQ1}),1.0]])]});}
            var Q27;
            {var subQ0=sQuery(id+"F2.wireOp",EDGE,"E60.10");var subQ1=sQuery(id+"F2.wireOp",EDGE,"E53");var subQ2=makeQuery(id+"F2.imprint","INTERSECT",VERTEX,{"disambiguationData":[OD(0.0)],"derivedFrom":[subQ1,subQ0]});Q27=makeQuery(id+"F2.imprint","IMPRINT",FACE,{"disambiguationData":[TD([[makeQuery(id+"F2.imprint","IMPRINT",EDGE,{"disambiguationData":[TD([[subQ2,-1.0]])],"derivedFrom":subQ1}),1.0]])]});}
            var Q28;
            {var subQ0=sQuery(id+"F2.wireOp",EDGE,"E60.0");var subQ1=sQuery(id+"F2.wireOp",EDGE,"E54");var subQ2=makeQuery(id+"F2.imprint","INTERSECT",VERTEX,{"disambiguationData":[OD(0.0)],"derivedFrom":[subQ1,subQ0]});Q28=makeQuery(id+"F2.imprint","IMPRINT",FACE,{"disambiguationData":[TD([[makeQuery(id+"F2.imprint","IMPRINT",EDGE,{"disambiguationData":[TD([[subQ2,-1.0]])],"derivedFrom":subQ1}),-1.0]])]});}
            extrude(context, id + "F3", {"entities" : qUnion([Q0, Q1, Q2, Q3, Q4, Q5, Q6, Q7, Q8, Q9, Q10, Q11, Q12, Q13, Q14, Q15, Q16, Q17, Q18, Q19, Q20, Q21, Q22, Q23, Q24, Q25, Q26, Q27, Q28]), "depth" : 25.4 * mm});
        }
    });
